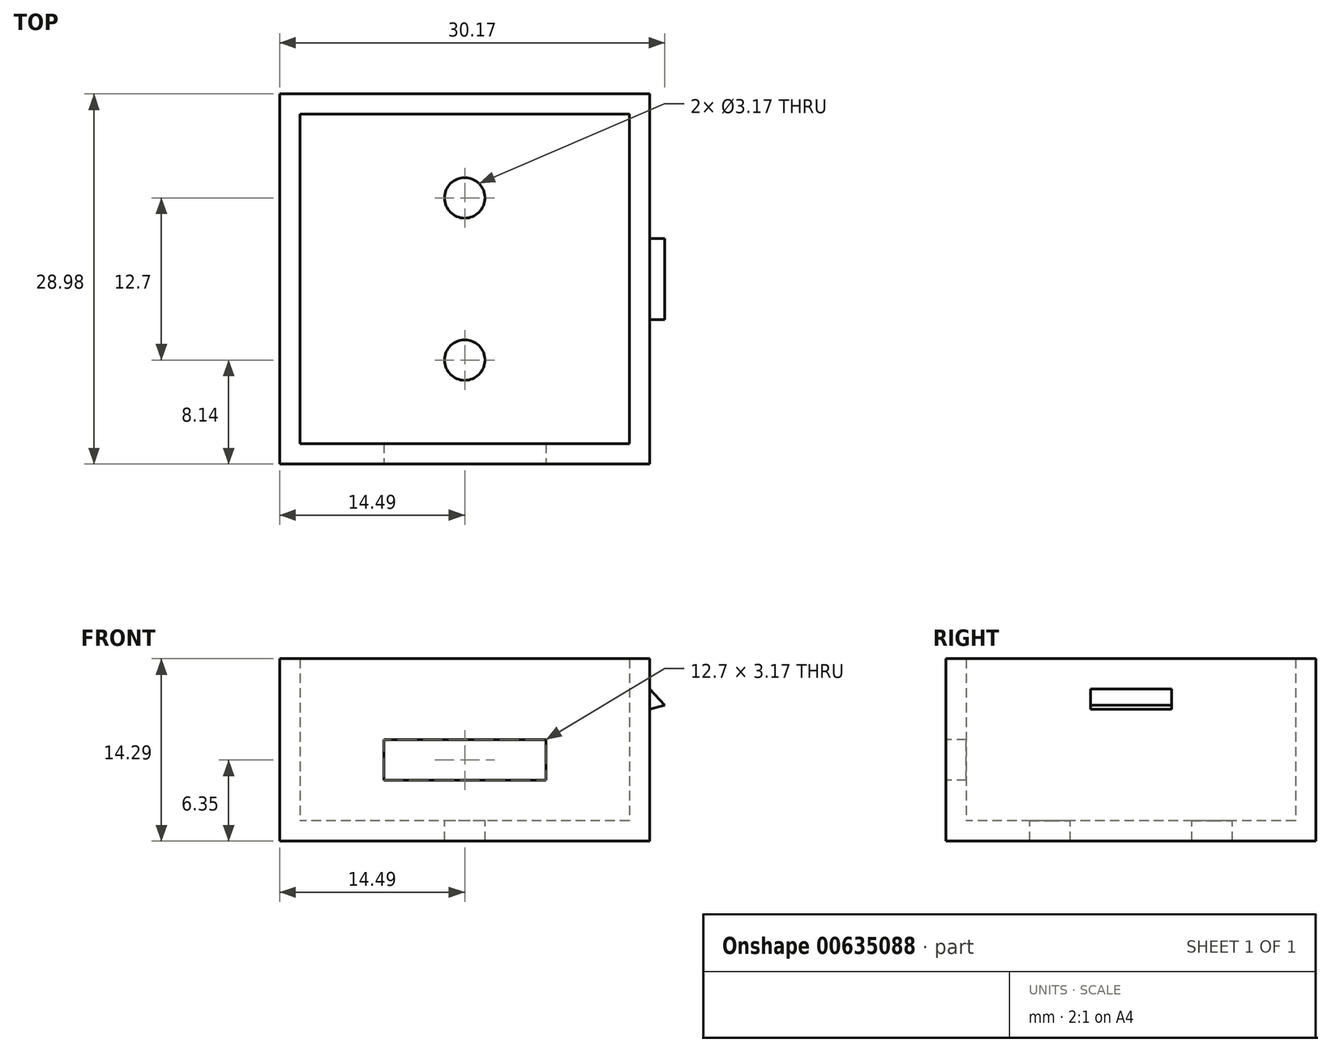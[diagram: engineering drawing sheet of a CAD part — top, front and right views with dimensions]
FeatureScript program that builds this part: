
annotation { "Feature Type Name" : "Feature", "Feature Type Description" : "" }
export const myFeature = defineFeature(function(context is Context, id is Id, definition is map)
    precondition{}
    {
        {
            var Q0;
            Q0=qCreatedBy(makeId("Top.planeOp"),FACE);
            var sketch = newSketch(context, id + "F0", { "sketchPlane" : qUnion([Q0])});
            skLineSegment(sketch, "E0.bottom", {"start": v(12.9, 12.9) * mm, "end": v(-12.9, 12.9) * mm});
            skLineSegment(sketch, "E0.top", {"start": v(12.9, -12.9) * mm, "end": v(-12.9, -12.9) * mm});
            skLineSegment(sketch, "E0.left", {"start": v(12.9, 12.9) * mm, "end": v(12.9, -12.9) * mm});
            skLineSegment(sketch, "E0.right", {"start": v(-12.9, 12.9) * mm, "end": v(-12.9, -12.9) * mm});
            skPoint(sketch, "E0.middle", {"position": v(0, 0) * mm});
            skLineSegment(sketch, "E1.bottom", {"start": v(14.49, 14.49) * mm, "end": v(-14.49, 14.49) * mm});
            skLineSegment(sketch, "E1.top", {"start": v(14.49, -14.49) * mm, "end": v(-14.49, -14.49) * mm});
            skLineSegment(sketch, "E1.left", {"start": v(14.49, 14.49) * mm, "end": v(14.49, -14.49) * mm});
            skLineSegment(sketch, "E1.right", {"start": v(-14.49, 14.49) * mm, "end": v(-14.49, -14.49) * mm});
            skSolve(sketch);
        }
        {
            var Q0;
            Q0 = qSketchRegion(id + "F0", true);
            extrude(context, id + "F1", {"entities" : qUnion([Q0]), "depth" : 14.29 * mm, "offsetDistance" : 25.4 * mm});
        }
        {
            var Q0;
            Q0=makeQuery(id+"F1.opExtrude","CAP_FACE",FACE,{"disambiguationData":[OSD([sQuery(id+"F0.wireOp",EDGE,"E0.bottom"),sQuery(id+"F0.wireOp",EDGE,"E0.top"),sQuery(id+"F0.wireOp",EDGE,"E0.left"),sQuery(id+"F0.wireOp",EDGE,"E0.right"),sQuery(id+"F0.wireOp",EDGE,"E1.bottom"),sQuery(id+"F0.wireOp",EDGE,"E1.top"),sQuery(id+"F0.wireOp",EDGE,"E1.left"),sQuery(id+"F0.wireOp",EDGE,"E1.right")])],"isStart":true});
            var sketch = newSketch(context, id + "F2", { "sketchPlane" : qUnion([Q0])});
            skLineSegment(sketch, "E2.bottom", {"start": v(12.9, 12.9) * mm, "end": v(-12.9, 12.9) * mm});
            skLineSegment(sketch, "E2.top", {"start": v(12.9, -12.9) * mm, "end": v(-12.9, -12.9) * mm});
            skLineSegment(sketch, "E2.left", {"start": v(12.9, 12.9) * mm, "end": v(12.9, -12.9) * mm});
            skLineSegment(sketch, "E2.right", {"start": v(-12.9, 12.9) * mm, "end": v(-12.9, -12.9) * mm});
            skPoint(sketch, "E2.middle", {"position": v(0, 0) * mm});
            skSolve(sketch);
        }
        {
            var Q0;
            Q0=makeQuery(id+"F2.imprint","IMPRINT",FACE,{"disambiguationData":[TD([[makeQuery(id+"F2.imprint","IMPRINT",EDGE,{"derivedFrom":sQuery(id+"F2.wireOp",EDGE,"E2.bottom")}),1.0]])]});
            extrude(context, id + "F3", {"entities" : qUnion([Q0]), "oppositeDirection" : true, "depth" : 1.59 * mm, "offsetDistance" : 25.4 * mm});
        }
        {
            var Q0;
            Q0=makeQuery(id+"F1.opExtrude","SWEPT_BODY",BODY,{"disambiguationData":[OSD([sQuery(id+"F0.wireOp",EDGE,"E0.bottom"),sQuery(id+"F0.wireOp",EDGE,"E0.top"),sQuery(id+"F0.wireOp",EDGE,"E0.left"),sQuery(id+"F0.wireOp",EDGE,"E0.right"),sQuery(id+"F0.wireOp",EDGE,"E1.bottom"),sQuery(id+"F0.wireOp",EDGE,"E1.top"),sQuery(id+"F0.wireOp",EDGE,"E1.left"),sQuery(id+"F0.wireOp",EDGE,"E1.right")])]});
            var Q1;
            Q1=makeQuery(id+"F3.opExtrude","SWEPT_BODY",BODY,{"disambiguationData":[OSD([sQuery(id+"F2.wireOp",EDGE,"E2.bottom"),sQuery(id+"F2.wireOp",EDGE,"E2.top"),sQuery(id+"F2.wireOp",EDGE,"E2.left"),sQuery(id+"F2.wireOp",EDGE,"E2.right")])]});
            booleanBodies(context, id + "F4", {"operationType" : BooleanOperationType.UNION, "tools" : qUnion([Q0, Q1])});
        }
        {
            var Q0;
            Q0=qCreatedBy(makeId("Front.planeOp"),FACE);
            var sketch = newSketch(context, id + "F5", { "sketchPlane" : qUnion([Q0])});
            skLineSegment(sketch, "E3", {"start": v(14.49, 10.32) * mm, "end": v(14.49, 11.9) * mm});
            skLineSegment(sketch, "E4", {"start": v(14.49, 11.9) * mm, "end": v(15.68, 10.64) * mm});
            skLineSegment(sketch, "E5", {"start": v(15.68, 10.64) * mm, "end": v(14.49, 10.32) * mm});
            skPoint(sketch, "E6", {"position": v(14.49, 11.11) * mm});
            skSolve(sketch);
        }
        {
            var Q0;
            Q0 = qSketchRegion(id + "F5", true);
            extrude(context, id + "F6", {"entities" : qUnion([Q0]), "operationType" : NewBodyOperationType.ADD, "endBound" : BoundingType.SYMMETRIC, "depth" : 6.35 * mm, "offsetDistance" : 25.4 * mm});
        }
        {
            var Q0;
            Q0=qCreatedBy(makeId("Front.planeOp"),FACE);
            var sketch = newSketch(context, id + "F7", { "sketchPlane" : qUnion([Q0])});
            skLineSegment(sketch, "E7", {"start": v(0, 0) * mm, "end": v(0, 14.29) * mm});
            skSolve(sketch);
        }
        {
            var Q0;
            Q0=makeQuery(id+"F3.opExtrude","CAP_FACE",FACE,{"disambiguationData":[OSD([sQuery(id+"F2.wireOp",EDGE,"E2.bottom"),sQuery(id+"F2.wireOp",EDGE,"E2.top"),sQuery(id+"F2.wireOp",EDGE,"E2.left"),sQuery(id+"F2.wireOp",EDGE,"E2.right")])],"isStart":false});
            var sketch = newSketch(context, id + "F8", { "sketchPlane" : qUnion([Q0])});
            skCircle(sketch, "E8", {"center": v(0, 6.35) * mm, "radius": 1.59 * mm});
            skCircle(sketch, "E9", {"center": v(0, -6.35) * mm, "radius": 1.59 * mm});
            skSolve(sketch);
        }
        {
            var Q0;
            Q0 = qSketchRegion(id + "F8", true);
            extrude(context, id + "F9", {"entities" : qUnion([Q0]), "operationType" : NewBodyOperationType.REMOVE, "endBound" : BoundingType.THROUGH_ALL, "oppositeDirection" : true, "depth" : 25.4 * mm, "offsetDistance" : 25.4 * mm});
        }
        {
            var Q0;
            Q0=makeQuery(id+"F1.opExtrude","SWEPT_FACE",FACE,{"disambiguationData":[OSD([sQuery(id+"F0.wireOp",EDGE,"E1.top")])]});
            var sketch = newSketch(context, id + "F10", { "sketchPlane" : qUnion([Q0])});
            skLineSegment(sketch, "E10.bottom", {"start": v(6.35, 7.94) * mm, "end": v(-6.35, 7.94) * mm});
            skLineSegment(sketch, "E10.top", {"start": v(6.35, 4.76) * mm, "end": v(-6.35, 4.76) * mm});
            skLineSegment(sketch, "E10.left", {"start": v(6.35, 7.94) * mm, "end": v(6.35, 4.76) * mm});
            skLineSegment(sketch, "E10.right", {"start": v(-6.35, 7.94) * mm, "end": v(-6.35, 4.76) * mm});
            skPoint(sketch, "E10.middle", {"position": v(0, 6.35) * mm});
            skSolve(sketch);
        }
        {
            var Q0;
            Q0 = qSketchRegion(id + "F10", true);
            extrude(context, id + "F11", {"entities" : qUnion([Q0]), "operationType" : NewBodyOperationType.REMOVE, "endBound" : BoundingType.UP_TO_NEXT, "oppositeDirection" : true, "depth" : 25.4 * mm, "offsetDistance" : 25.4 * mm});
        }
    });
